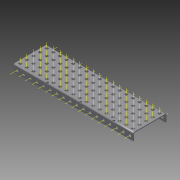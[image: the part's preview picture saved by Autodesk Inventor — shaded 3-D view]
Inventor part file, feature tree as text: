
AUTODESK INVENTOR PART (.ipt)
format: ipt  version: 2015 (Build 190159000, 159)  size: 2,660,352 bytes
history: native  units: in
note: dims shown in document units (in); Inventor stores cm internally (conversion verified against a paired STEP export)
features: other x132, pattern_linear x2, sheet_metal_op x1, extrude x1, imported_body x1, sketch x1
ambient origin geometry x8: Origin, YZ Plane, XZ Plane, XY Plane, X Axis, Y Axis, Z Axis, Center Point
bodies: Body1 (feature_tree)
feature tree (138):
  sheet_metal_op  "Fold1"
  other  "C-Channel"
  extrude  "length cut"  Depth=0.5in
  other  "top axis"
  other  "front axis"
  other  "back axis"
  pattern_linear  "top axes"  Spacing1=0.5in  [1 undecoded]
  pattern_linear  "horiz axes"  Spacing1=0.0in  [1 undecoded]
  other  "right plane"
  imported_body  "Base1"
  sketch  "Sketch1"  dims[d1=0.0in d4=0.5in d5=1.9685in d7=0.5in d10=0.5in d11=0.0in d12=0.0in d13=0.0in d14=-9.0in d15=0.0in d16=0.0in]
  other  "Work Point1"
  other  "Work Axis6"
  other  "Work Axis11"
  other  "Work Axis16"
  other  "Work Axis21"
  other  "Work Point2"
  other  "Work Point3"
  other  "Work Axis36"
  other  "Work Axis37"
  other  "Work Axis38"
  other  "Work Axis39"
  other  "Work Axis40"
  other  "Work Axis41"
  other  "Work Axis60"
  other  "Work Axis61"
  other  "Work Axis62"
  other  "Work Axis63"
  other  "Work Axis64"
  other  "Work Axis65"
  other  "Work Axis84"
  other  "Work Axis85"
  other  "Work Axis86"
  other  "Work Axis87"
  other  "Work Axis88"
  other  "Work Axis89"
  other  "Work Axis108"
  other  "Work Axis109"
  other  "Work Axis110"
  other  "Work Axis111"
  other  "Work Axis112"
  other  "Work Axis113"
  other  "Work Axis132"
  other  "Work Axis133"
  other  "Work Axis134"
  other  "Work Axis135"
  other  "Work Axis136"
  other  "Work Axis137"
  other  "Work Axis156"
  other  "Work Axis157"
  other  "Work Axis158"
  other  "Work Axis159"
  other  "Work Axis160"
  other  "Work Axis161"
  other  "Work Axis180"
  other  "Work Axis181"
  other  "Work Axis182"
  other  "Work Axis183"
  other  "Work Axis184"
  other  "Work Axis185"
  other  "Work Axis204"
  other  "Work Axis205"
  other  "Work Axis206"
  other  "Work Axis207"
  other  "Work Axis208"
  other  "Work Axis209"
  other  "Work Axis210"
  other  "Work Axis211"
  other  "Work Axis212"
  other  "Work Axis213"
  other  "Work Axis214"
  other  "Work Axis232"
  other  "Work Axis233"
  other  "Work Axis234"
  other  "Work Axis235"
  other  "Work Axis236"
  other  "Work Axis237"
  other  "Work Axis238"
  other  "Work Axis239"
  other  "Work Axis240"
  other  "Work Axis241"
  other  "Work Axis242"
  other  "Work Axis260"
  other  "Work Axis261"
  other  "Work Axis262"
  other  "Work Axis263"
  other  "Work Axis264"
  other  "Work Axis265"
  other  "Work Axis266"
  other  "Work Axis267"
  other  "Work Axis268"
  other  "Work Axis269"
  other  "Work Axis270"
  other  "Work Axis288"
  other  "Work Axis289"
  other  "Work Axis290"
  other  "Work Axis291"
  other  "Work Axis292"
  other  "Work Axis293"
  other  "Work Axis294"
  other  "Work Axis295"
  other  "Work Axis296"
  other  "Work Axis297"
  other  "Work Axis298"
  other  "Work Axis316"
  other  "Work Axis317"
  other  "Work Axis318"
  other  "Work Axis319"
  other  "Work Axis320"
  other  "Work Axis321"
  other  "Work Axis322"
  other  "Work Axis323"
  other  "Work Axis324"
  other  "Work Axis325"
  other  "Work Axis326"
  other  "Work Axis344"
  other  "Work Axis345"
  other  "Work Axis346"
  other  "Work Axis347"
  other  "Work Axis348"
  other  "Work Axis349"
  other  "Work Axis350"
  other  "Work Axis351"
  other  "Work Axis352"
  other  "Work Axis353"
  other  "Work Axis354"
  other  "Work Axis372"
  other  "Work Axis373"
  other  "Work Axis374"
  other  "Work Axis375"
  other  "Work Axis376"
  other  "Work Axis377"
  other  "Work Axis378"
  other  "Work Axis379"
  other  "Work Axis380"
  other  "Work Axis381"
  other  "Work Axis382"
  other  "left plane"
note: 2 required parameter values undecoded (feature->parameter linkage not recoverable at this tier; creation-order binding heuristic only, values carry confidence <= 0.55)
